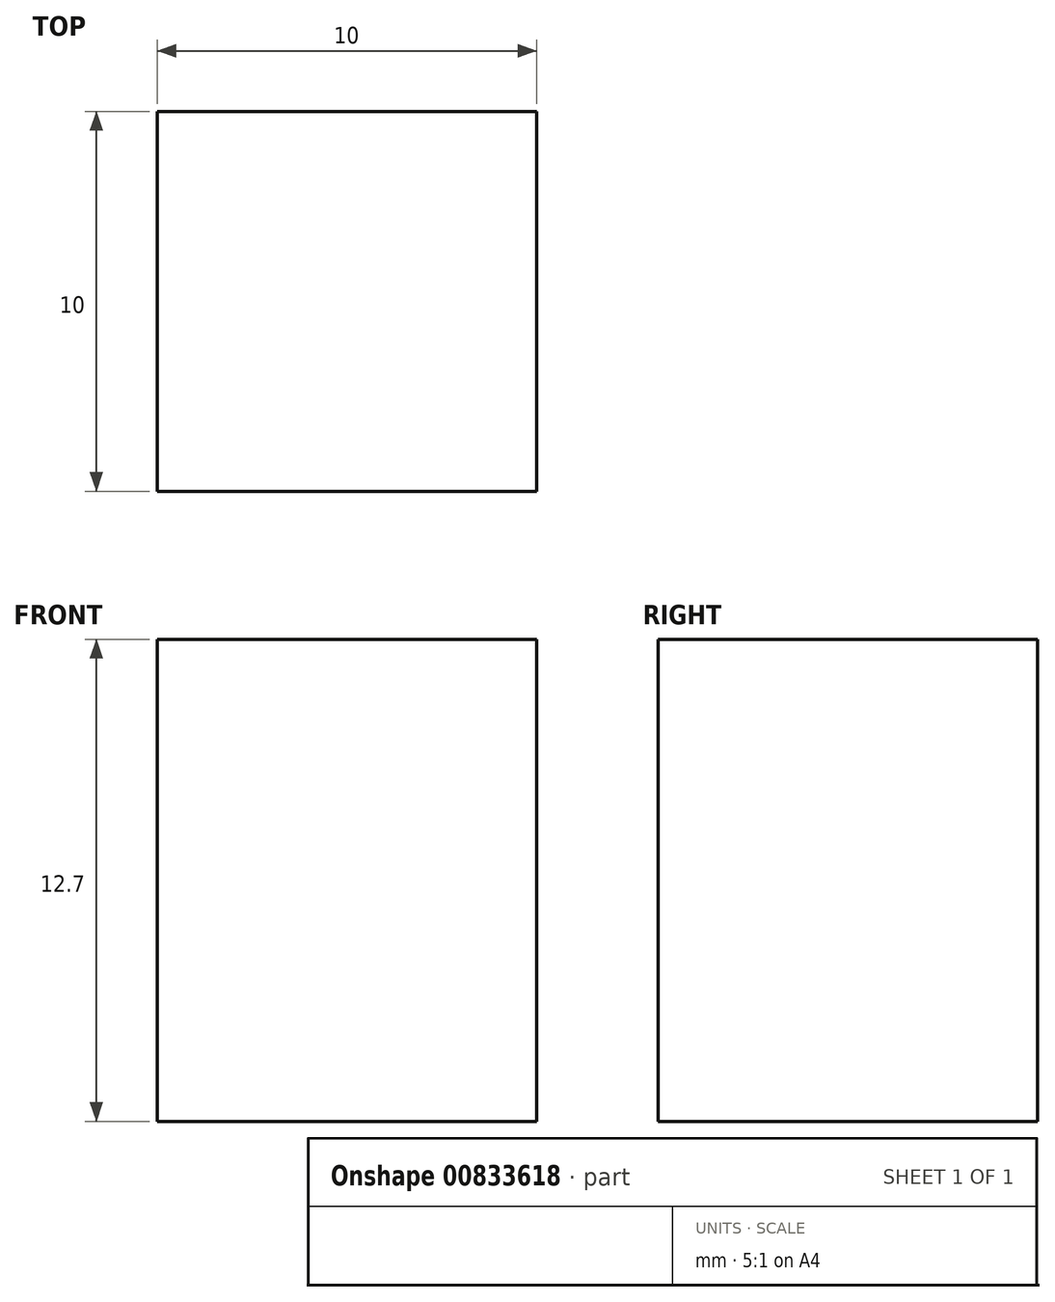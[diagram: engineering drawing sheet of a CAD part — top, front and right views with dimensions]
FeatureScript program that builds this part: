
annotation { "Feature Type Name" : "Feature", "Feature Type Description" : "" }
export const myFeature = defineFeature(function(context is Context, id is Id, definition is map)
    precondition{}
    {
        {
            var Q0;
            Q0=qCreatedBy(makeId("Top.planeOp"),FACE);
            var sketch = newSketch(context, id + "F0", { "sketchPlane" : qUnion([Q0])});
            skLineSegment(sketch, "E0", {"start": v(0, 0) * mm, "end": v(10, 0) * mm});
            skLineSegment(sketch, "E1", {"start": v(10, 0) * mm, "end": v(10, 10) * mm});
            skLineSegment(sketch, "E2", {"start": v(10, 10) * mm, "end": v(0, 10) * mm});
            skLineSegment(sketch, "E3", {"start": v(0, 10) * mm, "end": v(0, 0) * mm});
            skSolve(sketch);
        }
        {
            var Q0;
            Q0=makeQuery(id+"F0.imprint","IMPRINT",FACE,{"disambiguationData":[TD([[makeQuery(id+"F0.imprint","IMPRINT",EDGE,{"derivedFrom":sQuery(id+"F0.wireOp",EDGE,"E0")}),1.0]])]});
            extrude(context, id + "F1", {"entities" : qUnion([Q0]), "depth" : 12.7 * mm, "offsetDistance" : 25 * mm});
        }
    });
